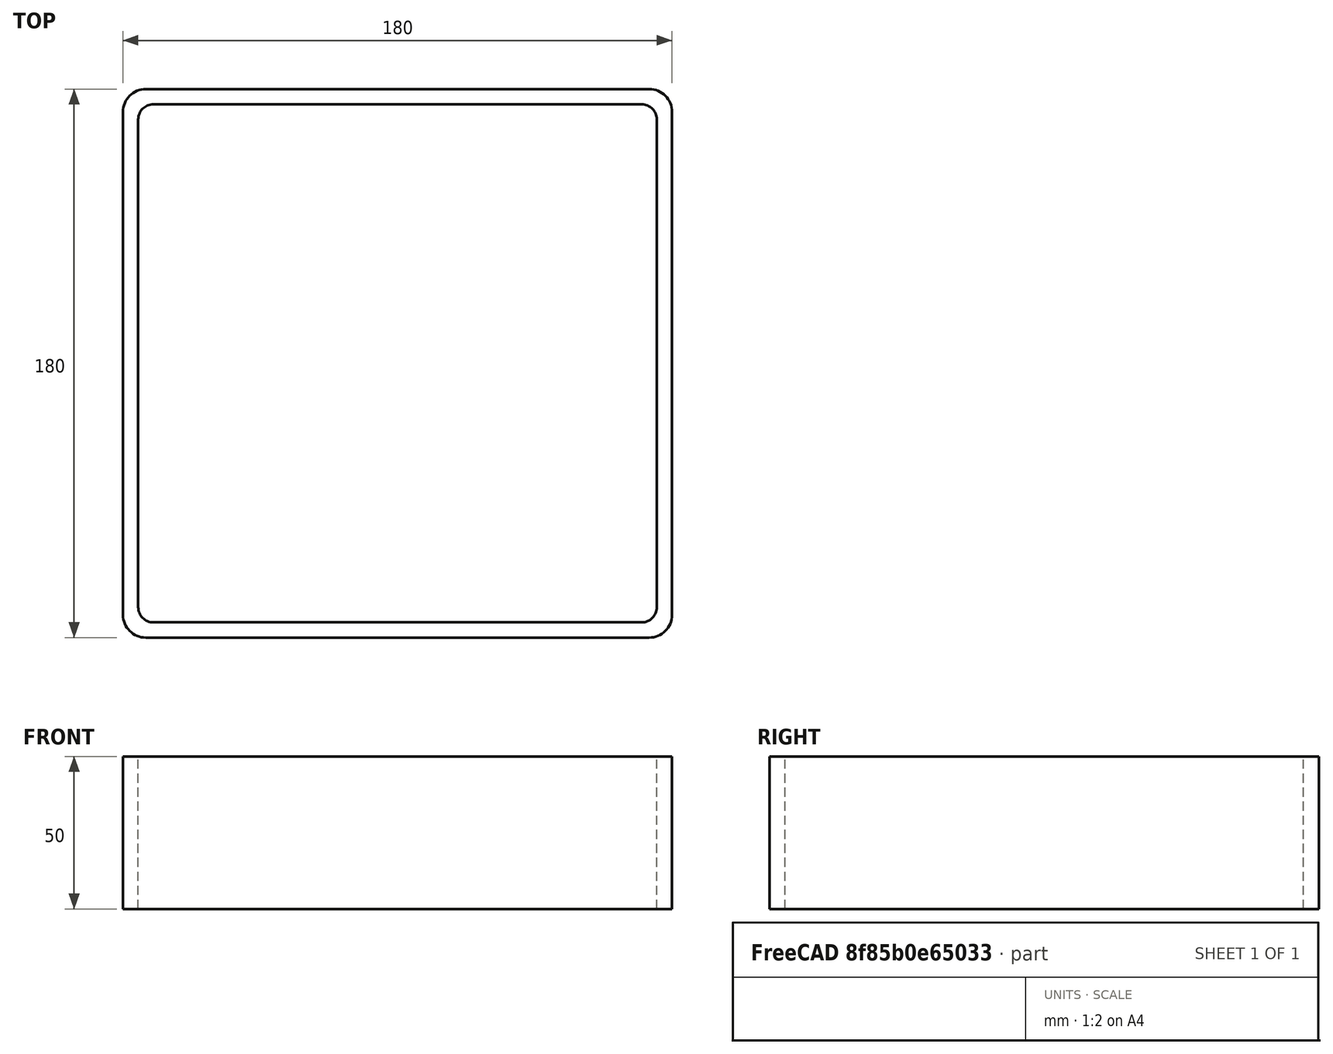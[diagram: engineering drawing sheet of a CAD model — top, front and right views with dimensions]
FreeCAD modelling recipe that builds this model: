
FCSTD DOCUMENT  (FreeCAD 0.15R4671 (Git))
Label: Square hollow section 180x180x5 EN10219 S235JRH
License: All rights reserved
LicenseURL: http://en.wikipedia.org/wiki/All_rights_reserved
objects: Sketcher::SketchObject×1, Part::Extrusion×1
note: 2 computed .brp shape members not serialized (recipe doc carries the construction recipe); baked Part::Feature solids carry a one-line shape summary decoded from their .brp

FEATURE [Sketcher::SketchObject] Sketch
  sketch-geometry (16):
    g0: LineSegment StartX=-80 StartY=85 StartZ=0 EndX=80 EndY=85 EndZ=0
    g1: LineSegment StartX=85 StartY=80 StartZ=0 EndX=85 EndY=-80 EndZ=0
    g2: LineSegment StartX=80 StartY=-85 StartZ=0 EndX=-80 EndY=-85 EndZ=0
    g3: LineSegment StartX=-85 StartY=-80 StartZ=0 EndX=-85 EndY=80 EndZ=0
    g4: LineSegment StartX=-82.5 StartY=90 StartZ=0 EndX=82.5 EndY=90 EndZ=0
    g5: LineSegment StartX=90 StartY=82.5 StartZ=0 EndX=90 EndY=-82.5 EndZ=0
    g6: LineSegment StartX=82.5 StartY=-90 StartZ=0 EndX=-82.5 EndY=-90 EndZ=0
    g7: LineSegment StartX=-90 StartY=-82.5 StartZ=0 EndX=-90 EndY=82.5 EndZ=0
    g8: ArcOfCircle CenterX=-80 CenterY=80 CenterZ=0 NormalX=0 NormalY=0 NormalZ=1 Radius=5 StartAngle=1.5708 EndAngle=3.14159
    g9: ArcOfCircle CenterX=80 CenterY=80 CenterZ=0 NormalX=0 NormalY=0 NormalZ=1 Radius=5 StartAngle=0 EndAngle=1.5708
    g10: ArcOfCircle CenterX=80 CenterY=-80 CenterZ=0 NormalX=0 NormalY=0 NormalZ=1 Radius=5 StartAngle=4.71239 EndAngle=6.28319
    g11: ArcOfCircle CenterX=-80 CenterY=-80 CenterZ=0 NormalX=0 NormalY=0 NormalZ=1 Radius=5 StartAngle=3.14159 EndAngle=4.71239
    g12: ArcOfCircle CenterX=82.5 CenterY=82.5 CenterZ=0 NormalX=0 NormalY=0 NormalZ=1 Radius=7.5 StartAngle=0 EndAngle=1.5708
    g13: ArcOfCircle CenterX=82.5 CenterY=-82.5 CenterZ=0 NormalX=0 NormalY=0 NormalZ=1 Radius=7.5 StartAngle=4.71239 EndAngle=6.28319
    g14: ArcOfCircle CenterX=-82.5 CenterY=-82.5 CenterZ=0 NormalX=0 NormalY=0 NormalZ=1 Radius=7.5 StartAngle=3.14159 EndAngle=4.71239
    g15: ArcOfCircle CenterX=-82.5 CenterY=82.5 CenterZ=0 NormalX=0 NormalY=0 NormalZ=1 Radius=7.5 StartAngle=1.5708 EndAngle=3.14159
  constraints (36):
    c: Horizontal(g2)
    c: Vertical(g3)
    c: Horizontal(g6)
    c: Vertical(g7)
    c: Tangent(g3,g8) = 1.5708
    c: Tangent(g0,g8) = 1.5708
    c: Tangent(g0,g9) = 1.5708
    c: Tangent(g1,g9) = 1.5708
    c: Tangent(g1,g10) = 1.5708
    c: Tangent(g2,g10) = 1.5708
    c: Tangent(g2,g11) = 1.5708
    c: Tangent(g3,g11) = 1.5708
    c: Tangent(g4,g12) = 1.5708
    c: Tangent(g5,g12) = 1.5708
    c: Tangent(g5,g13) = 1.5708
    c: Tangent(g6,g13) = 1.5708
    c: Tangent(g6,g14) = 1.5708
    c: Tangent(g7,g14) = 1.5708
    c: Tangent(g7,g15) = 1.5708
    c: Tangent(g4,g15) = 1.5708
    c: Equal(g9,g8)
    c: Equal(g9,g11)
    c: Equal(g9,g10)
    c: Equal(g12,g15)
    c: Equal(g12,g14)
    c: Equal(g12,g13)
    c: Symmetric(g4,g6,g-1)
    c: Symmetric(g7,g5,g-2)
    c: DistanceY(g4,g6) = -180
    c: DistanceX(g7,g5) = 180
    c: Symmetric(g3,g1,g-2)
    c: Symmetric(g0,g2,g-1)
    c: DistanceY(g0,g4) = 5
    c: DistanceX(g5,g1) = -5
    c: Radius(g9) = 5
    c: Radius(g12) = 7.5
FEATURE [Part::Extrusion] Extrude  label="Square hollow section 180x180x5 EN10219 S235JRH"
  Base = -> Sketch
  Dir = (0,0,50)
  Solid = true
